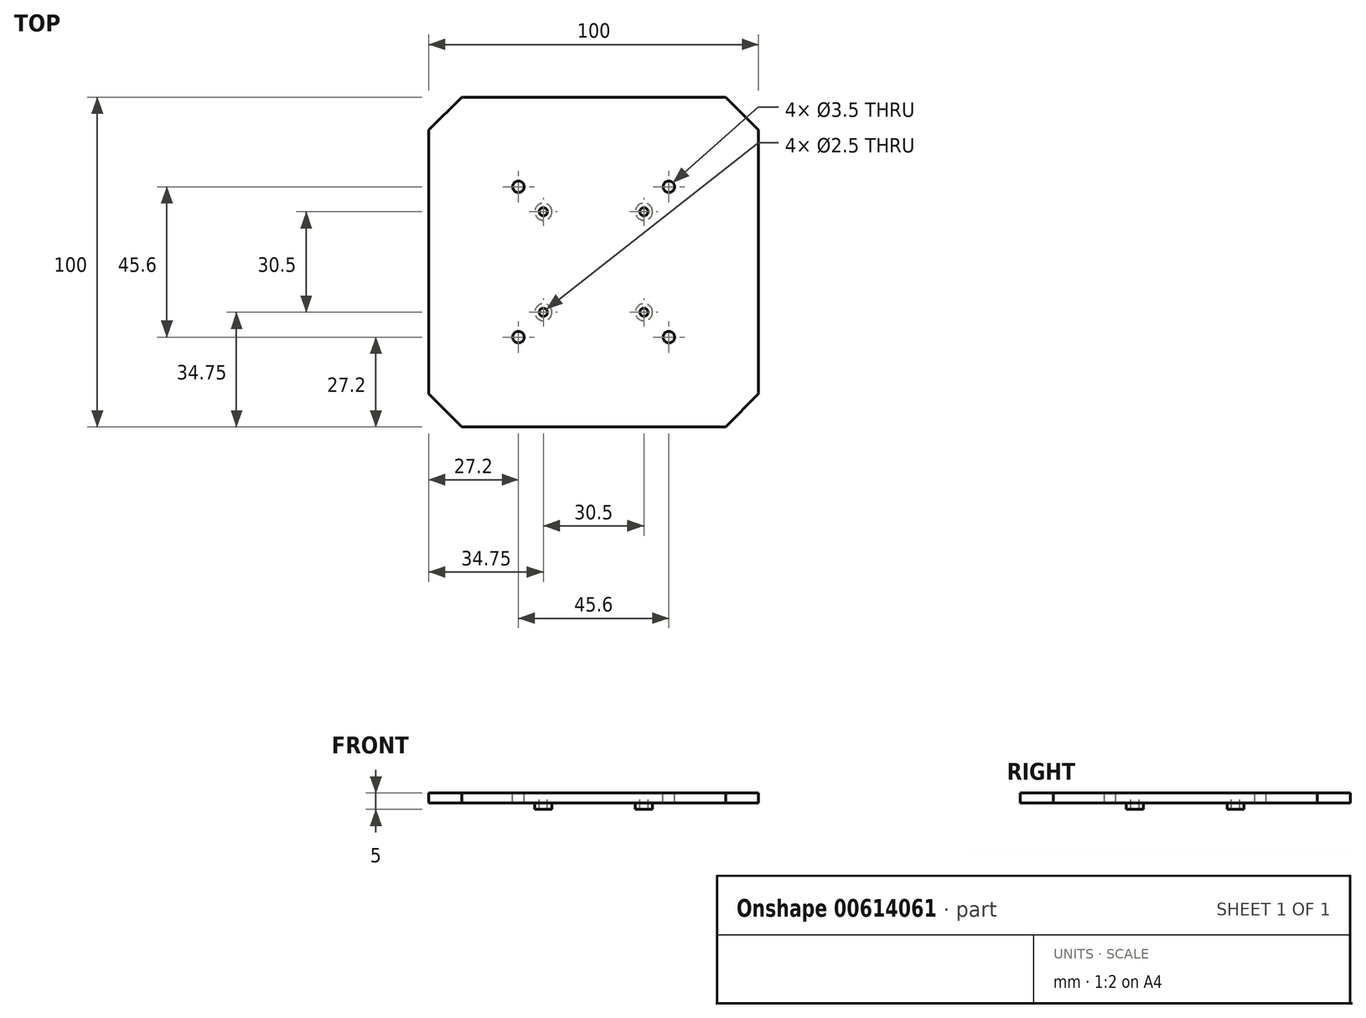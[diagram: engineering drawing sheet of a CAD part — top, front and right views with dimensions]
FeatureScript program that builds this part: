
annotation { "Feature Type Name" : "Feature", "Feature Type Description" : "" }
export const myFeature = defineFeature(function(context is Context, id is Id, definition is map)
    precondition{}
    {
        {
            var Q0;
            Q0=qCreatedBy(makeId("Top.planeOp"),FACE);
            var sketch = newSketch(context, id + "F0", { "sketchPlane" : qUnion([Q0])});
            skPoint(sketch, "E0.middle", {"position": v(0, 0) * mm});
            skLineSegment(sketch, "E1.bottom", {"start": v(22.8, -22.8) * mm, "end": v(-22.8, -22.8) * mm});
            skLineSegment(sketch, "E1.top", {"start": v(22.8, 22.8) * mm, "end": v(-22.8, 22.8) * mm});
            skLineSegment(sketch, "E1.left", {"start": v(22.8, -22.8) * mm, "end": v(22.8, 22.8) * mm});
            skLineSegment(sketch, "E1.right", {"start": v(-22.8, -22.8) * mm, "end": v(-22.8, 22.8) * mm});
            skLineSegment(sketch, "E2.bottom", {"start": v(15.25, -15.25) * mm, "end": v(-15.25, -15.25) * mm});
            skLineSegment(sketch, "E2.top", {"start": v(15.25, 15.25) * mm, "end": v(-15.25, 15.25) * mm});
            skLineSegment(sketch, "E2.left", {"start": v(15.25, -15.25) * mm, "end": v(15.25, 15.25) * mm});
            skLineSegment(sketch, "E2.right", {"start": v(-15.25, -15.25) * mm, "end": v(-15.25, 15.25) * mm});
            skCircle(sketch, "E3", {"center": v(-22.8, 22.8) * mm, "radius": 1.75 * mm});
            skCircle(sketch, "E4", {"center": v(22.8, 22.8) * mm, "radius": 1.75 * mm});
            skCircle(sketch, "E5", {"center": v(22.8, -22.8) * mm, "radius": 1.75 * mm});
            skCircle(sketch, "E6", {"center": v(-22.8, -22.8) * mm, "radius": 1.75 * mm});
            skLineSegment(sketch, "E7.bottom", {"start": v(50, -50) * mm, "end": v(-50, -50) * mm});
            skLineSegment(sketch, "E7.top", {"start": v(50, 50) * mm, "end": v(-50, 50) * mm});
            skLineSegment(sketch, "E7.left", {"start": v(50, -50) * mm, "end": v(50, 50) * mm});
            skLineSegment(sketch, "E7.right", {"start": v(-50, -50) * mm, "end": v(-50, 50) * mm});
            skCircle(sketch, "E8", {"center": v(-15.25, 15.25) * mm, "radius": 2.6 * mm});
            skCircle(sketch, "E9", {"center": v(15.25, 15.25) * mm, "radius": 2.6 * mm});
            skCircle(sketch, "E10", {"center": v(15.25, -15.25) * mm, "radius": 2.6 * mm});
            skCircle(sketch, "E11", {"center": v(-15.25, -15.25) * mm, "radius": 2.6 * mm});
            skSolve(sketch);
        }
        {
            var Q0;
            Q0=makeQuery(id+"F0.imprint","IMPRINT",FACE,{"disambiguationData":[TD([[makeQuery(id+"F0.imprint","IMPRINT",EDGE,{"derivedFrom":sQuery(id+"F0.wireOp",EDGE,"E7.bottom")}),-1.0]])]});
            var Q1;
            {var subQ21=sQuery(id+"F0.wireOp",EDGE,"E5");var subQ22=sQuery(id+"F0.wireOp",EDGE,"E1.bottom");var subQ23=makeQuery(id+"F0.imprint","INTERSECT",VERTEX,{"derivedFrom":[subQ22,subQ21]});Q1=makeQuery(id+"F0.imprint","IMPRINT",FACE,{"disambiguationData":[TD([[makeQuery(id+"F0.imprint","IMPRINT",EDGE,{"disambiguationData":[TD([[subQ23,-1.0]])],"derivedFrom":subQ22}),-1.0]])]});}
            var Q2;
            {var subQ5=sQuery(id+"F0.wireOp",EDGE,"E10");var subQ13=sQuery(id+"F0.wireOp",EDGE,"E2.bottom");var subQ14=makeQuery(id+"F0.imprint","INTERSECT",VERTEX,{"derivedFrom":[subQ13,subQ5]});Q2=makeQuery(id+"F0.imprint","IMPRINT",FACE,{"disambiguationData":[TD([[makeQuery(id+"F0.imprint","IMPRINT",EDGE,{"disambiguationData":[TD([[subQ14,-1.0]])],"derivedFrom":subQ13}),-1.0]])]});}
            extrude(context, id + "F1", {"entities" : qUnion([Q0, Q1, Q2]), "oppositeDirection" : true, "depth" : 3 * mm, "offsetDistance" : 25 * mm});
        }
        {
            var Q0;
            {var subQ0=sQuery(id+"F0.wireOp",EDGE,"E2.right");var subQ1=sQuery(id+"F0.wireOp",EDGE,"E2.bottom");var subQ2=makeQuery(id+"F0.imprint","INTERSECT",VERTEX,{"derivedFrom":[subQ1,subQ0]});Q0=makeQuery(id+"F0.imprint","IMPRINT",FACE,{"disambiguationData":[TD([[makeQuery(id+"F0.imprint","IMPRINT",EDGE,{"disambiguationData":[TD([[subQ2,1.0]])],"derivedFrom":subQ1}),-1.0]])]});}
            var Q1;
            {var subQ0=sQuery(id+"F0.wireOp",EDGE,"E2.right");var subQ1=sQuery(id+"F0.wireOp",EDGE,"E2.bottom");var subQ2=makeQuery(id+"F0.imprint","INTERSECT",VERTEX,{"derivedFrom":[subQ1,subQ0]});Q1=makeQuery(id+"F0.imprint","IMPRINT",FACE,{"disambiguationData":[TD([[makeQuery(id+"F0.imprint","IMPRINT",EDGE,{"disambiguationData":[TD([[subQ2,1.0]])],"derivedFrom":subQ1}),1.0]])]});}
            var Q2;
            {var subQ0=sQuery(id+"F0.wireOp",EDGE,"E2.left");var subQ1=sQuery(id+"F0.wireOp",EDGE,"E2.bottom");var subQ2=makeQuery(id+"F0.imprint","INTERSECT",VERTEX,{"derivedFrom":[subQ1,subQ0]});Q2=makeQuery(id+"F0.imprint","IMPRINT",FACE,{"disambiguationData":[TD([[makeQuery(id+"F0.imprint","IMPRINT",EDGE,{"disambiguationData":[TD([[subQ2,-1.0]])],"derivedFrom":subQ1}),1.0]])]});}
            var Q3;
            {var subQ0=sQuery(id+"F0.wireOp",EDGE,"E2.left");var subQ1=sQuery(id+"F0.wireOp",EDGE,"E2.bottom");var subQ2=makeQuery(id+"F0.imprint","INTERSECT",VERTEX,{"derivedFrom":[subQ1,subQ0]});Q3=makeQuery(id+"F0.imprint","IMPRINT",FACE,{"disambiguationData":[TD([[makeQuery(id+"F0.imprint","IMPRINT",EDGE,{"disambiguationData":[TD([[subQ2,-1.0]])],"derivedFrom":subQ1}),-1.0]])]});}
            var Q4;
            {var subQ0=sQuery(id+"F0.wireOp",EDGE,"E2.right");var subQ1=sQuery(id+"F0.wireOp",EDGE,"E2.top");var subQ2=makeQuery(id+"F0.imprint","INTERSECT",VERTEX,{"derivedFrom":[subQ1,subQ0]});Q4=makeQuery(id+"F0.imprint","IMPRINT",FACE,{"disambiguationData":[TD([[makeQuery(id+"F0.imprint","IMPRINT",EDGE,{"disambiguationData":[TD([[subQ2,1.0]])],"derivedFrom":subQ1}),1.0]])]});}
            var Q5;
            {var subQ0=sQuery(id+"F0.wireOp",EDGE,"E2.right");var subQ1=sQuery(id+"F0.wireOp",EDGE,"E2.top");var subQ2=makeQuery(id+"F0.imprint","INTERSECT",VERTEX,{"derivedFrom":[subQ1,subQ0]});Q5=makeQuery(id+"F0.imprint","IMPRINT",FACE,{"disambiguationData":[TD([[makeQuery(id+"F0.imprint","IMPRINT",EDGE,{"disambiguationData":[TD([[subQ2,1.0]])],"derivedFrom":subQ1}),-1.0]])]});}
            var Q6;
            {var subQ0=sQuery(id+"F0.wireOp",EDGE,"E2.left");var subQ1=sQuery(id+"F0.wireOp",EDGE,"E2.top");var subQ2=makeQuery(id+"F0.imprint","INTERSECT",VERTEX,{"derivedFrom":[subQ1,subQ0]});Q6=makeQuery(id+"F0.imprint","IMPRINT",FACE,{"disambiguationData":[TD([[makeQuery(id+"F0.imprint","IMPRINT",EDGE,{"disambiguationData":[TD([[subQ2,-1.0]])],"derivedFrom":subQ1}),1.0]])]});}
            var Q7;
            {var subQ0=sQuery(id+"F0.wireOp",EDGE,"E2.left");var subQ1=sQuery(id+"F0.wireOp",EDGE,"E2.top");var subQ2=makeQuery(id+"F0.imprint","INTERSECT",VERTEX,{"derivedFrom":[subQ1,subQ0]});Q7=makeQuery(id+"F0.imprint","IMPRINT",FACE,{"disambiguationData":[TD([[makeQuery(id+"F0.imprint","IMPRINT",EDGE,{"disambiguationData":[TD([[subQ2,-1.0]])],"derivedFrom":subQ1}),-1.0]])]});}
            extrude(context, id + "F2", {"entities" : qUnion([Q0, Q1, Q2, Q3, Q4, Q5, Q6, Q7]), "operationType" : NewBodyOperationType.ADD, "oppositeDirection" : true, "depth" : 5 * mm, "offsetDistance" : 25 * mm});
        }
        {
            var Q0;
            Q0=sQuery(id+"F0.wireOp",VERTEX,"E2.bottom.end");
            var Q1;
            Q1=sQuery(id+"F0.wireOp",VERTEX,"E2.top.end");
            var Q2;
            Q2=sQuery(id+"F0.wireOp",VERTEX,"E9.center");
            var Q3;
            Q3=sQuery(id+"F0.wireOp",VERTEX,"E10.center");
            var Q4;
            Q4=makeQuery(id+"F1.opExtrude","SWEPT_BODY",BODY,{"disambiguationData":[OSD([sQuery(id+"F0.wireOp",EDGE,"E3"),sQuery(id+"F0.wireOp",EDGE,"E4"),sQuery(id+"F0.wireOp",EDGE,"E5"),sQuery(id+"F0.wireOp",EDGE,"E6"),sQuery(id+"F0.wireOp",EDGE,"E7.bottom"),sQuery(id+"F0.wireOp",EDGE,"E7.top"),sQuery(id+"F0.wireOp",EDGE,"E7.left"),sQuery(id+"F0.wireOp",EDGE,"E7.right"),sQuery(id+"F0.wireOp",EDGE,"E8"),sQuery(id+"F0.wireOp",EDGE,"E9"),sQuery(id+"F0.wireOp",EDGE,"E10"),sQuery(id+"F0.wireOp",EDGE,"E11")])]});
            hole(context, id + "F3", {"style" : HoleStyle.SIMPLE, "endStyle" : HoleEndStyle.BLIND, "holeDiameter" : 2.5 * mm, "majorDiameter" : 5 * mm, "holeDepth" : 6 * mm, "isTappedThrough" : true, "tappedDepth" : 12 * mm, "tapClearance" : 3, "locations" : qUnion([Q0, Q1, Q2, Q3]), "scope" : qUnion([Q4])});
        }
        {
            var Q0;
            Q0=makeQuery(id+"F1.opExtrude","SWEPT_EDGE",EDGE,{"disambiguationData":[OSD([sQuery(id+"F0.wireOp",EDGE,"E7.top"),sQuery(id+"F0.wireOp",EDGE,"E7.right")])]});
            var Q1;
            Q1=makeQuery(id+"F1.opExtrude","SWEPT_EDGE",EDGE,{"disambiguationData":[OSD([sQuery(id+"F0.wireOp",EDGE,"E7.top"),sQuery(id+"F0.wireOp",EDGE,"E7.left")])]});
            var Q2;
            Q2=makeQuery(id+"F1.opExtrude","SWEPT_EDGE",EDGE,{"disambiguationData":[OSD([sQuery(id+"F0.wireOp",EDGE,"E7.bottom"),sQuery(id+"F0.wireOp",EDGE,"E7.left")])]});
            var Q3;
            Q3=makeQuery(id+"F1.opExtrude","SWEPT_EDGE",EDGE,{"disambiguationData":[OSD([sQuery(id+"F0.wireOp",EDGE,"E7.bottom"),sQuery(id+"F0.wireOp",EDGE,"E7.right")])]});
            chamfer(context, id + "F4", {"entities" : qUnion([Q0, Q1, Q2, Q3]), "width" : 10 * mm, "tangentPropagation" : true});
        }
    });
